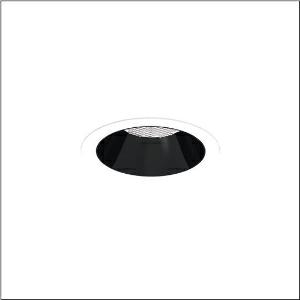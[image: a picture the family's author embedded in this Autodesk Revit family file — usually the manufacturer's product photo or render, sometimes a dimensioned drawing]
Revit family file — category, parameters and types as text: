
# Revit family: lunis_21_l_51db17ed91c
name_source: partatom
category: Lighting Fixtures
units: mm (PartAtom-declared; Revit-internal decimal feet)

## family parameters
Cut with Voids When Loaded = No
Host = Face
Light Source = No
Part Type = Normal
Room Calculation Point = No
Round Connector Dimension = Use Diameter
Shared = No

## types (1)
- --- (1 x LED, 3470 lm, 25.4 W, 4000K)
    Apparent Load = 25 VA
    CIE Flux Codes = 90 99 100 100 100
    Color Rendering = 80
    Color Temperature = 4000K
    Default Elevation = 1800 mm
    Description = Lunis 21,  L, downlight, light control with lens, of PMMA, anti glare with reflector, of PC, light emission: direct distribution, LED rated luminous flux: 1.790lm, light colour: 830/840/865, with terminal, 5-pole, mains connection: 220..240V, AC/DC, 0/50..60Hz, housing, round, of diecast aluminium, traffic white (RAL 9016), diameter: 165mm, clamping range: 1..40mm, protection rating (complete): IP20, protection rating (on room side): IP54, insulation class (complete): insulation class II (safety insulation), certification: CE, impact resistance: IK03, packaging unit: 1 piece
    Height = 0 mm  [stored 0 ft]
    Lamp = 1 x LED
    Lamp Light Flux = 3470 lm
    Lamp Power = 25.4 W
    Lamp count = 1
    Length = 165 mm
    Luminous efficacy = 137 lm/W
    Manufacturer = Siteco
    ModVariant = No
    Model = 51DB17ED91C
    Mounting Place = Ceiling
    Mounting Type = Recessed
    Number of Poles = 1
    OnlyDefault = Yes
    Power Factor = 1
    Product Name = Lunis 21 L
    Product group = downlight
    ProductGroupID = 400
    Protection Class = Protection class II
    Protection Degree = IP 20
    RLX_Detail_Level = 1
    RLX_Emergency_Light_Flux = 0 lm
    RLX_Emergency_Type = 0
    RLX_Emergency_Type_DB = No
    RlxData = <blob elided: 15113 chars, md5=59be22f4>
    Socket = socket
    Standby Power = 0 W
    System Light Flux = 3470 lm
    System Power = 25 W
    Type Comments = individual setting: colour temperature 4000K, luminous flux: 100 % | (ON | ON | OFF | OFF) | 700 mA
    Type Image = l_1291094.jpg
    URL = http://relux.com
    VarID = @adj_022221
    Voltage = 0 V
    Weight = 0.00 kg
    Width = 0 mm  [stored 0 ft]

note: [stored X ft] marks values corroborated as IEEE doubles in the binary element streams (Revit-internal decimal feet)

## geometry (parser evidence)
native form markers: Sweep x10
no freeform markers — native parametric forms only
